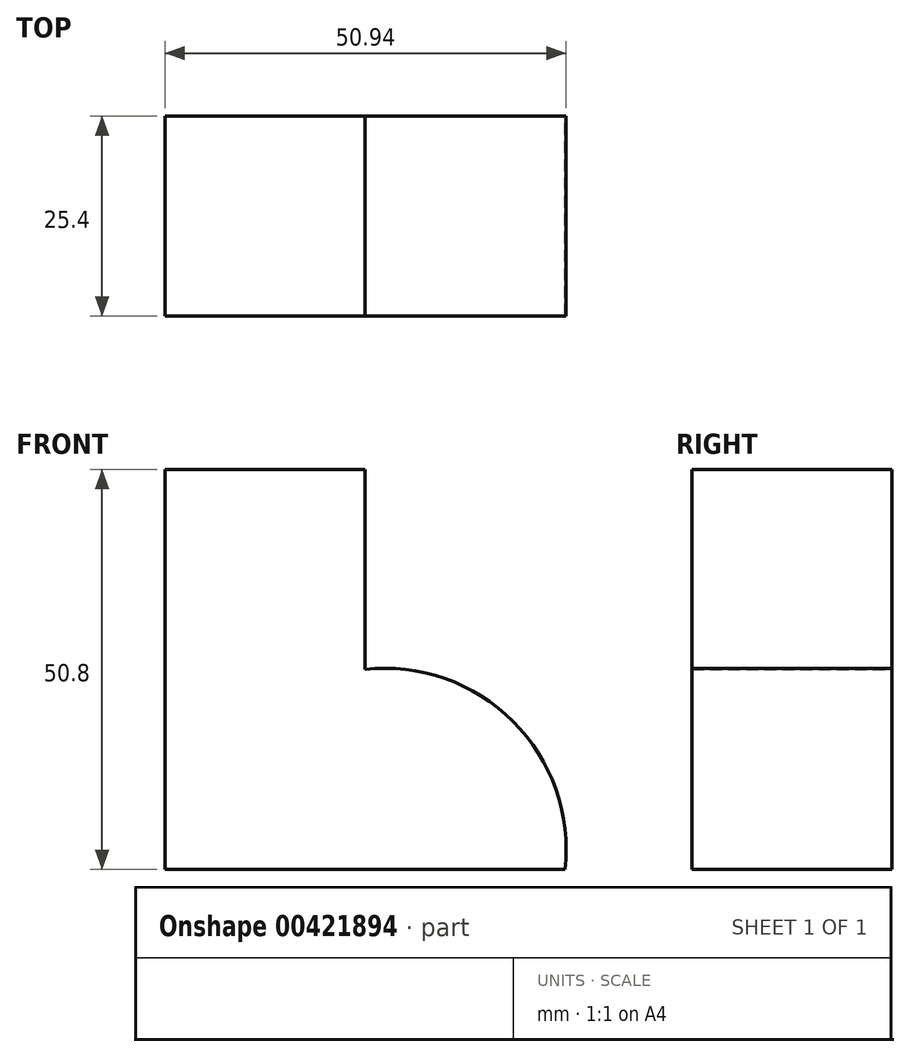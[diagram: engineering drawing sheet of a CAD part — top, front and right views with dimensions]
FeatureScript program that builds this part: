
annotation { "Feature Type Name" : "Feature", "Feature Type Description" : "" }
export const myFeature = defineFeature(function(context is Context, id is Id, definition is map)
    precondition{}
    {
        {
            var Q0;
            Q0=qCreatedBy(makeId("Front.planeOp"),FACE);
            var sketch = newSketch(context, id + "F0", { "sketchPlane" : qUnion([Q0])});
            skLineSegment(sketch, "E0", {"start": v(0, 0) * mm, "end": v(-50.8, 0) * mm});
            skLineSegment(sketch, "E1", {"start": v(-50.8, 0) * mm, "end": v(-50.8, 50.8) * mm});
            skLineSegment(sketch, "E2", {"start": v(-50.8, 50.8) * mm, "end": v(-25.4, 50.8) * mm});
            skLineSegment(sketch, "E3", {"start": v(-25.4, 50.8) * mm, "end": v(-25.4, 25.4) * mm});
            skArc(sketch, "E4", {"start": v(0, 0) * mm, "mid": v(-6.6, 18.8) * mm, "end": v(-25.4, 25.4) * mm});
            skSolve(sketch);
        }
        {
            var Q0;
            Q0=makeQuery(id+"F0.imprint","IMPRINT",FACE,{"disambiguationData":[TD([[makeQuery(id+"F0.imprint","IMPRINT",EDGE,{"derivedFrom":sQuery(id+"F0.wireOp",EDGE,"E0")}),-1.0]])]});
            extrude(context, id + "F1", {"entities" : qUnion([Q0]), "depth" : 25.4 * mm});
        }
    });
